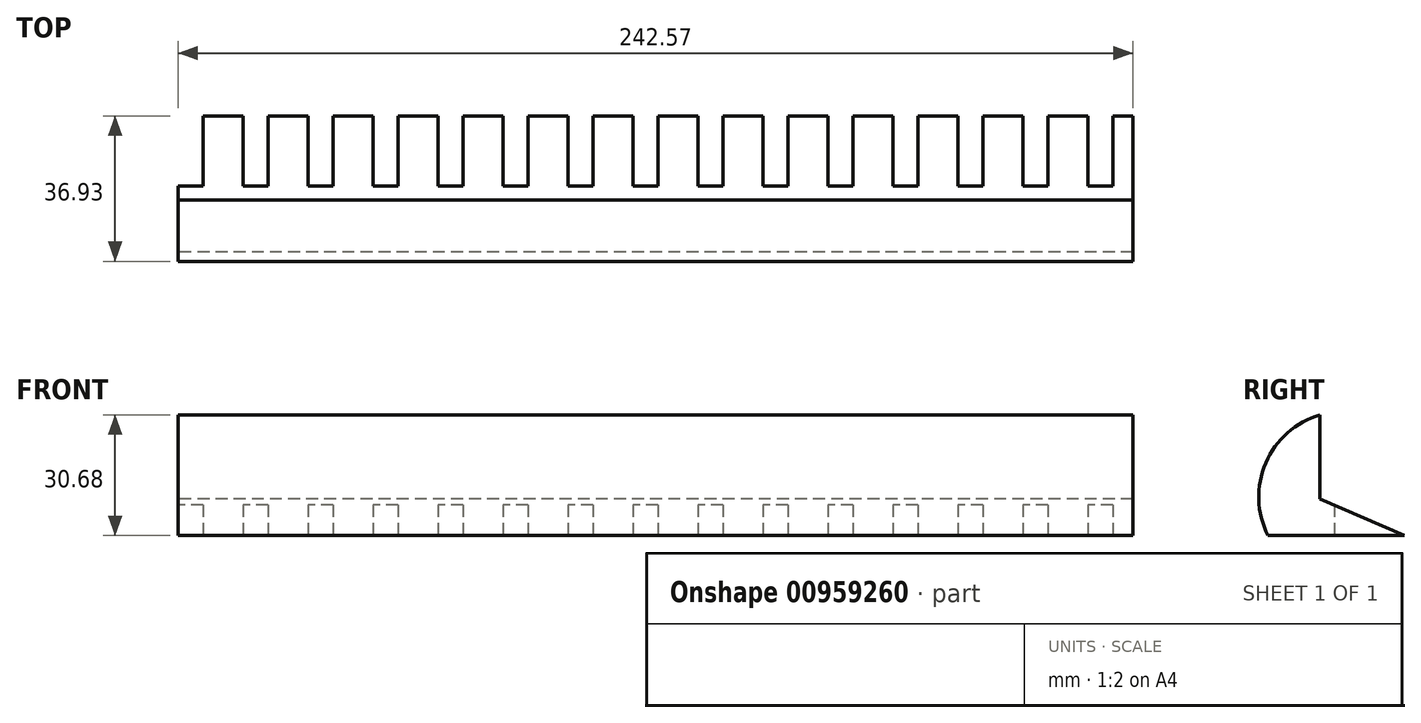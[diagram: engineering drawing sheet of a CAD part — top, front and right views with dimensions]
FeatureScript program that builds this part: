
annotation { "Feature Type Name" : "Feature", "Feature Type Description" : "" }
export const myFeature = defineFeature(function(context is Context, id is Id, definition is map)
    precondition{}
    {
        {
            var Q0;
            Q0=qCreatedBy(makeId("Right.planeOp"),FACE);
            var sketch = newSketch(context, id + "F0", { "sketchPlane" : qUnion([Q0])});
            skLineSegment(sketch, "E0", {"start": v(0, 9.32) * mm, "end": v(0, 30.68) * mm});
            skLineSegment(sketch, "E1", {"start": v(0, 9.32) * mm, "end": v(21.36, 0) * mm});
            skLineSegment(sketch, "E2", {"start": v(21.36, 0) * mm, "end": v(-13.21, 0) * mm});
            skArc(sketch, "E3", {"start": v(0, 30.68) * mm, "mid": v(-13.8, 18.44) * mm, "end": v(-13.21, 0) * mm});
            skSolve(sketch);
        }
        {
            var Q0;
            Q0=makeQuery(id+"F0.imprint","IMPRINT",FACE,{"disambiguationData":[TD([[makeQuery(id+"F0.imprint","IMPRINT",EDGE,{"derivedFrom":sQuery(id+"F0.wireOp",EDGE,"E0")}),1.0]])]});
            extrude(context, id + "F1", {"entities" : qUnion([Q0]), "depth" : 242.57 * mm, "offsetDistance" : 25.4 * mm});
        }
        {
            var Q0;
            Q0=makeQuery(id+"F1.opExtrude","SWEPT_FACE",FACE,{"disambiguationData":[OSD([sQuery(id+"F0.wireOp",EDGE,"E2")])]});
            var sketch = newSketch(context, id + "F2", { "sketchPlane" : qUnion([Q0])});
            skLineSegment(sketch, "E4.bottom", {"start": v(0, -21.36) * mm, "end": v(6.35, -21.36) * mm});
            skLineSegment(sketch, "E4.top", {"start": v(0, -3.58) * mm, "end": v(6.35, -3.58) * mm});
            skLineSegment(sketch, "E4.left", {"start": v(0, -21.36) * mm, "end": v(0, -3.58) * mm});
            skLineSegment(sketch, "E4.right", {"start": v(6.35, -21.36) * mm, "end": v(6.35, -3.58) * mm});
            skLineSegment(sketch, "E5.bottom", {"start": v(16.51, -21.36) * mm, "end": v(22.86, -21.36) * mm});
            skLineSegment(sketch, "E5.top", {"start": v(16.51, -3.58) * mm, "end": v(22.86, -3.58) * mm});
            skLineSegment(sketch, "E5.left", {"start": v(16.51, -21.36) * mm, "end": v(16.51, -3.58) * mm});
            skLineSegment(sketch, "E5.right", {"start": v(22.86, -21.36) * mm, "end": v(22.86, -3.58) * mm});
            skLineSegment(sketch, "E6.bottom", {"start": v(33.02, -21.36) * mm, "end": v(39.37, -21.36) * mm});
            skLineSegment(sketch, "E6.top", {"start": v(33.02, -3.58) * mm, "end": v(39.37, -3.58) * mm});
            skLineSegment(sketch, "E6.left", {"start": v(33.02, -21.36) * mm, "end": v(33.02, -3.58) * mm});
            skLineSegment(sketch, "E6.right", {"start": v(39.37, -21.36) * mm, "end": v(39.37, -3.58) * mm});
            skLineSegment(sketch, "E7.bottom", {"start": v(49.53, -21.36) * mm, "end": v(55.88, -21.36) * mm});
            skLineSegment(sketch, "E7.top", {"start": v(49.53, -3.58) * mm, "end": v(55.88, -3.58) * mm});
            skLineSegment(sketch, "E7.left", {"start": v(49.53, -21.36) * mm, "end": v(49.53, -3.58) * mm});
            skLineSegment(sketch, "E7.right", {"start": v(55.88, -21.36) * mm, "end": v(55.88, -3.58) * mm});
            skLineSegment(sketch, "E8.bottom", {"start": v(66.04, -21.36) * mm, "end": v(72.4, -21.36) * mm});
            skLineSegment(sketch, "E8.top", {"start": v(66.04, -3.58) * mm, "end": v(72.4, -3.58) * mm});
            skLineSegment(sketch, "E8.left", {"start": v(66.04, -21.36) * mm, "end": v(66.04, -3.58) * mm});
            skLineSegment(sketch, "E8.right", {"start": v(72.4, -21.36) * mm, "end": v(72.4, -3.58) * mm});
            skLineSegment(sketch, "E9.bottom", {"start": v(82.55, -21.36) * mm, "end": v(88.9, -21.36) * mm});
            skLineSegment(sketch, "E9.top", {"start": v(82.55, -3.58) * mm, "end": v(88.9, -3.58) * mm});
            skLineSegment(sketch, "E9.left", {"start": v(82.55, -21.36) * mm, "end": v(82.55, -3.58) * mm});
            skLineSegment(sketch, "E9.right", {"start": v(88.9, -21.36) * mm, "end": v(88.9, -3.58) * mm});
            skLineSegment(sketch, "E10.bottom", {"start": v(99.06, -21.36) * mm, "end": v(105.4, -21.36) * mm});
            skLineSegment(sketch, "E10.top", {"start": v(99.06, -3.58) * mm, "end": v(105.4, -3.58) * mm});
            skLineSegment(sketch, "E10.left", {"start": v(99.06, -21.36) * mm, "end": v(99.06, -3.58) * mm});
            skLineSegment(sketch, "E10.right", {"start": v(105.4, -21.36) * mm, "end": v(105.4, -3.58) * mm});
            skLineSegment(sketch, "E11.bottom", {"start": v(115.57, -21.36) * mm, "end": v(121.92, -21.36) * mm});
            skLineSegment(sketch, "E11.top", {"start": v(115.57, -3.58) * mm, "end": v(121.92, -3.58) * mm});
            skLineSegment(sketch, "E11.left", {"start": v(115.57, -21.36) * mm, "end": v(115.57, -3.58) * mm});
            skLineSegment(sketch, "E11.right", {"start": v(121.92, -21.36) * mm, "end": v(121.92, -3.58) * mm});
            skLineSegment(sketch, "E12.bottom", {"start": v(132.08, -21.36) * mm, "end": v(138.43, -21.36) * mm});
            skLineSegment(sketch, "E12.top", {"start": v(132.08, -3.58) * mm, "end": v(138.43, -3.58) * mm});
            skLineSegment(sketch, "E12.left", {"start": v(132.08, -21.36) * mm, "end": v(132.08, -3.58) * mm});
            skLineSegment(sketch, "E12.right", {"start": v(138.43, -21.36) * mm, "end": v(138.43, -3.58) * mm});
            skLineSegment(sketch, "E13.bottom", {"start": v(148.6, -21.36) * mm, "end": v(154.94, -21.36) * mm});
            skLineSegment(sketch, "E13.top", {"start": v(148.6, -3.58) * mm, "end": v(154.94, -3.58) * mm});
            skLineSegment(sketch, "E13.left", {"start": v(148.6, -21.36) * mm, "end": v(148.6, -3.58) * mm});
            skLineSegment(sketch, "E13.right", {"start": v(154.94, -21.36) * mm, "end": v(154.94, -3.58) * mm});
            skLineSegment(sketch, "E14.bottom", {"start": v(165.1, -21.36) * mm, "end": v(171.45, -21.36) * mm});
            skLineSegment(sketch, "E14.top", {"start": v(165.1, -3.58) * mm, "end": v(171.45, -3.58) * mm});
            skLineSegment(sketch, "E14.left", {"start": v(165.1, -21.36) * mm, "end": v(165.1, -3.58) * mm});
            skLineSegment(sketch, "E14.right", {"start": v(171.45, -21.36) * mm, "end": v(171.45, -3.58) * mm});
            skLineSegment(sketch, "E15.bottom", {"start": v(181.6, -21.36) * mm, "end": v(187.96, -21.36) * mm});
            skLineSegment(sketch, "E15.top", {"start": v(181.6, -3.58) * mm, "end": v(187.96, -3.58) * mm});
            skLineSegment(sketch, "E15.left", {"start": v(181.6, -21.36) * mm, "end": v(181.6, -3.58) * mm});
            skLineSegment(sketch, "E15.right", {"start": v(187.96, -21.36) * mm, "end": v(187.96, -3.58) * mm});
            skLineSegment(sketch, "E16.bottom", {"start": v(198.12, -21.36) * mm, "end": v(204.47, -21.36) * mm});
            skLineSegment(sketch, "E16.top", {"start": v(198.12, -3.58) * mm, "end": v(204.47, -3.58) * mm});
            skLineSegment(sketch, "E16.left", {"start": v(198.12, -21.36) * mm, "end": v(198.12, -3.58) * mm});
            skLineSegment(sketch, "E16.right", {"start": v(204.47, -21.36) * mm, "end": v(204.47, -3.58) * mm});
            skLineSegment(sketch, "E17.bottom", {"start": v(214.63, -21.36) * mm, "end": v(220.98, -21.36) * mm});
            skLineSegment(sketch, "E17.top", {"start": v(214.63, -3.58) * mm, "end": v(220.98, -3.58) * mm});
            skLineSegment(sketch, "E17.left", {"start": v(214.63, -21.36) * mm, "end": v(214.63, -3.58) * mm});
            skLineSegment(sketch, "E17.right", {"start": v(220.98, -21.36) * mm, "end": v(220.98, -3.58) * mm});
            skLineSegment(sketch, "E18.bottom", {"start": v(231.14, -21.36) * mm, "end": v(237.49, -21.36) * mm});
            skLineSegment(sketch, "E18.top", {"start": v(231.14, -3.58) * mm, "end": v(237.49, -3.58) * mm});
            skLineSegment(sketch, "E18.left", {"start": v(231.14, -21.36) * mm, "end": v(231.14, -3.58) * mm});
            skLineSegment(sketch, "E18.right", {"start": v(237.49, -21.36) * mm, "end": v(237.49, -3.58) * mm});
            skSolve(sketch);
        }
        {
            var Q0;
            Q0 = qSketchRegion(id + "F2", true);
            extrude(context, id + "F3", {"entities" : qUnion([Q0]), "operationType" : NewBodyOperationType.REMOVE, "endBound" : BoundingType.THROUGH_ALL, "oppositeDirection" : true, "depth" : 25.4 * mm, "offsetDistance" : 25.4 * mm});
        }
    });
